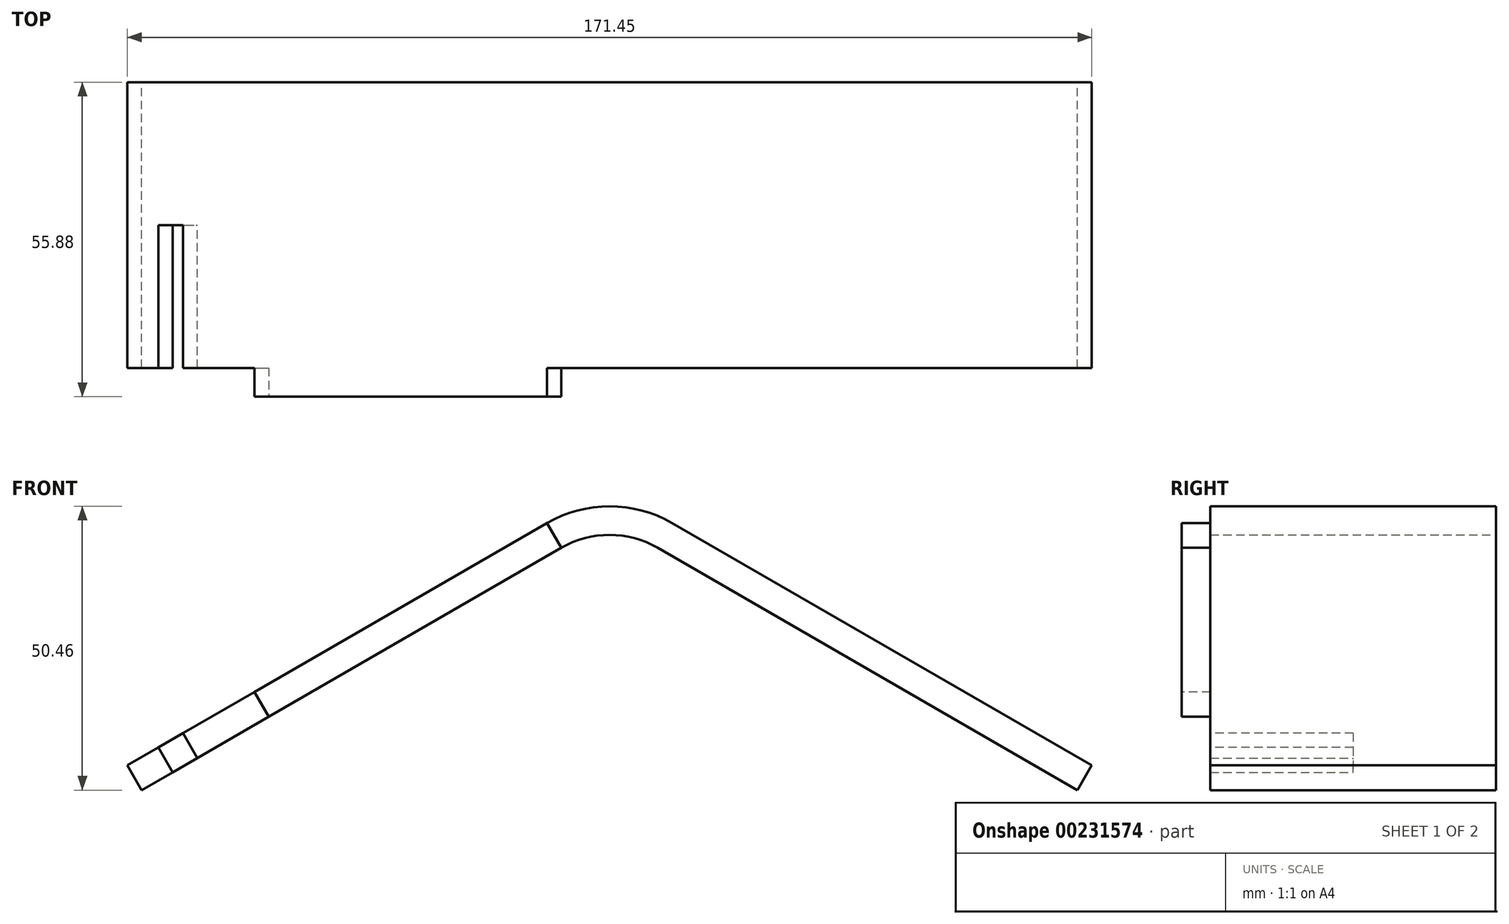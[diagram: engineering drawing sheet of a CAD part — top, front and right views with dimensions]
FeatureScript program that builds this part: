
annotation { "Feature Type Name" : "Feature", "Feature Type Description" : "" }
export const myFeature = defineFeature(function(context is Context, id is Id, definition is map)
    precondition{}
    {
        {
            var Q0;
            Q0=qCreatedBy(makeId("Front.planeOp"),FACE);
            var sketch = newSketch(context, id + "F0", { "sketchPlane" : qUnion([Q0])});
            skLineSegment(sketch, "E0", {"start": v(0, 0) * mm, "end": v(74.61, 43.08) * mm});
            skLineSegment(sketch, "E1", {"start": v(96.84, 43.08) * mm, "end": v(171.45, 0) * mm});
            skPoint(sketch, "E2.visualSharp", {"position": v(85.73, 49.5) * mm});
            skArc(sketch, "E2.filletArc", {"start": v(96.84, 43.08) * mm, "mid": v(85.73, 46.06) * mm, "end": v(74.61, 43.08) * mm});
            skLineSegment(sketch, "E3.0", {"start": v(94.3, 38.68) * mm, "end": v(168.91, -4.4) * mm});
            skArc(sketch, "E3.1", {"start": v(94.3, 38.68) * mm, "mid": v(85.73, 40.98) * mm, "end": v(77.15, 38.68) * mm});
            skLineSegment(sketch, "E3.2", {"start": v(2.54, -4.4) * mm, "end": v(77.15, 38.68) * mm});
            skLineSegment(sketch, "E4", {"start": v(2.54, -4.4) * mm, "end": v(0, 0) * mm});
            skLineSegment(sketch, "E5", {"start": v(168.91, -4.4) * mm, "end": v(171.45, 0) * mm});
            skSolve(sketch);
        }
        {
            var Q0;
            Q0=makeQuery(id+"F0.imprint","IMPRINT",FACE,{"disambiguationData":[TD([[makeQuery(id+"F0.imprint","IMPRINT",EDGE,{"derivedFrom":sQuery(id+"F0.wireOp",EDGE,"E0")}),-1.0]])]});
            extrude(context, id + "F1", {"entities" : qUnion([Q0]), "depth" : 50.8 * mm});
        }
        {
            var Q0;
            Q0=makeQuery(id+"F1.opExtrude","SWEPT_FACE",FACE,{"disambiguationData":[OSD([sQuery(id+"F0.wireOp",EDGE,"E4")])]});
            var Q1;
            Q1=makeQuery(id+"F1.opExtrude","SWEPT_FACE",FACE,{"disambiguationData":[OSD([sQuery(id+"F0.wireOp",EDGE,"E5")])]});
            cPlane(context, id + "F2", {"entities" : qUnion([Q0, Q1]), "cplaneType" : CPlaneType.MID_PLANE, "offset" : 25.4 * mm, "width" : 152.4 * mm, "height" : 152.4 * mm});
        }
        {
            var Q0;
            Q0=makeQuery(id+"F1.opExtrude","CAP_FACE",FACE,{"disambiguationData":[OSD([sQuery(id+"F0.wireOp",EDGE,"E0"),sQuery(id+"F0.wireOp",EDGE,"E1"),sQuery(id+"F0.wireOp",EDGE,"E2.filletArc"),sQuery(id+"F0.wireOp",EDGE,"E3.0"),sQuery(id+"F0.wireOp",EDGE,"E3.1"),sQuery(id+"F0.wireOp",EDGE,"E3.2"),sQuery(id+"F0.wireOp",EDGE,"E4"),sQuery(id+"F0.wireOp",EDGE,"E5")])],"isStart":false});
            var Q1;
            Q1=makeQuery(id+"F1.opExtrude","CAP_FACE",FACE,{"disambiguationData":[OSD([sQuery(id+"F0.wireOp",EDGE,"E0"),sQuery(id+"F0.wireOp",EDGE,"E1"),sQuery(id+"F0.wireOp",EDGE,"E2.filletArc"),sQuery(id+"F0.wireOp",EDGE,"E3.0"),sQuery(id+"F0.wireOp",EDGE,"E3.1"),sQuery(id+"F0.wireOp",EDGE,"E3.2"),sQuery(id+"F0.wireOp",EDGE,"E4"),sQuery(id+"F0.wireOp",EDGE,"E5")])],"isStart":true});
            cPlane(context, id + "F3", {"entities" : qUnion([Q0, Q1]), "cplaneType" : CPlaneType.MID_PLANE, "offset" : 25.4 * mm, "width" : 152.4 * mm, "height" : 152.4 * mm});
        }
        {
            var Q0;
            Q0=makeQuery(id+"F1.opExtrude","SWEPT_FACE",FACE,{"disambiguationData":[OSD([sQuery(id+"F0.wireOp",EDGE,"E3.2")])]});
            var sketch = newSketch(context, id + "F4", { "sketchPlane" : qUnion([Q0])});
            skLineSegment(sketch, "E6.bottom", {"start": v(86.16, 50.8) * mm, "end": v(26.09, 50.8) * mm});
            skLineSegment(sketch, "E6.top", {"start": v(86.16, 55.88) * mm, "end": v(26.09, 55.88) * mm});
            skLineSegment(sketch, "E6.left", {"start": v(86.16, 50.8) * mm, "end": v(86.16, 55.88) * mm});
            skLineSegment(sketch, "E6.right", {"start": v(26.09, 50.8) * mm, "end": v(26.09, 55.88) * mm});
            skSolve(sketch);
        }
        {
            var Q0;
            Q0=makeQuery(id+"F4.imprint","IMPRINT",FACE,{"disambiguationData":[TD([[makeQuery(id+"F4.imprint","IMPRINT",EDGE,{"derivedFrom":sQuery(id+"F4.wireOp",EDGE,"E6.bottom")}),1.0]])]});
            extrude(context, id + "F5", {"entities" : qUnion([Q0]), "operationType" : NewBodyOperationType.ADD, "oppositeDirection" : true, "depth" : 5.08 * mm});
        }
        {
            var Q0;
            {var subQ0=sQuery(id+"F4.wireOp",EDGE,"E6.right");var subQ1=sQuery(id+"F4.wireOp",EDGE,"E6.left");var subQ2=sQuery(id+"F4.wireOp",EDGE,"E6.top");var subQ3=sQuery(id+"F4.wireOp",EDGE,"E6.bottom");Q0=makeQuery(id+"FZIGQqVHOfLiniK_1.1.F5.boolean.opBoolean","MERGE",FACE,{"derivedFrom":[makeQuery(id+"F5.boolean.opBoolean","MERGE",FACE,{"derivedFrom":[makeQuery(id+"F1.opExtrude","SWEPT_FACE",FACE,{"disambiguationData":[OSD([sQuery(id+"F0.wireOp",EDGE,"E3.2")])]}),makeQuery(id+"F5.opExtrude","CAP_FACE",FACE,{"disambiguationData":[OSD([subQ3,subQ2,subQ1,subQ0])],"isStart":true})]}),makeQuery(id+"FZIGQqVHOfLiniK_1.1.F5.opExtrude","CAP_FACE",FACE,{"disambiguationData":[OSD([subQ3,subQ2,subQ1,subQ0])],"isStart":true})]});}
            var sketch = newSketch(context, id + "F6", { "sketchPlane" : qUnion([Q0])});
            skLineSegment(sketch, "E7.bottom", {"start": v(6.35, 50.8) * mm, "end": v(11.43, 50.8) * mm});
            skLineSegment(sketch, "E7.top", {"start": v(6.35, 25.4) * mm, "end": v(11.43, 25.4) * mm});
            skLineSegment(sketch, "E7.left", {"start": v(6.35, 50.8) * mm, "end": v(6.35, 25.4) * mm});
            skLineSegment(sketch, "E7.right", {"start": v(11.43, 50.8) * mm, "end": v(11.43, 25.4) * mm});
            skSolve(sketch);
        }
        {
            var Q0;
            Q0=makeQuery(id+"F6.imprint","IMPRINT",FACE,{"disambiguationData":[TD([[makeQuery(id+"F6.imprint","IMPRINT",EDGE,{"derivedFrom":sQuery(id+"F6.wireOp",EDGE,"E7.bottom")}),-1.0]])]});
            extrude(context, id + "F7", {"entities" : qUnion([Q0]), "operationType" : NewBodyOperationType.REMOVE, "endBound" : BoundingType.THROUGH_ALL, "oppositeDirection" : true, "depth" : 25.4 * mm});
        }
        {
            var Q0;
            {var subQ0=sQuery(id+"F4.wireOp",EDGE,"E6.right");var subQ1=sQuery(id+"F4.wireOp",EDGE,"E6.left");var subQ2=sQuery(id+"F4.wireOp",EDGE,"E6.top");var subQ3=sQuery(id+"F4.wireOp",EDGE,"E6.bottom");Q0=makeQuery(id+"FZIGQqVHOfLiniK_1.1.F5.boolean.opBoolean","MERGE",FACE,{"derivedFrom":[makeQuery(id+"F5.boolean.opBoolean","MERGE",FACE,{"derivedFrom":[makeQuery(id+"F1.opExtrude","SWEPT_FACE",FACE,{"disambiguationData":[OSD([sQuery(id+"F0.wireOp",EDGE,"E3.2")])]}),makeQuery(id+"F5.opExtrude","CAP_FACE",FACE,{"disambiguationData":[OSD([subQ3,subQ2,subQ1,subQ0])],"isStart":true})]}),makeQuery(id+"FZIGQqVHOfLiniK_1.1.F5.opExtrude","CAP_FACE",FACE,{"disambiguationData":[OSD([subQ3,subQ2,subQ1,subQ0])],"isStart":true})]});}
            var sketch = newSketch(context, id + "F8", { "sketchPlane" : qUnion([Q0])});
            skLineSegment(sketch, "E8.bottom", {"start": v(79.8, -5.08) * mm, "end": v(54.4, -5.08) * mm});
            skLineSegment(sketch, "E8.top", {"start": v(79.8, 0) * mm, "end": v(54.4, 0) * mm});
            skLineSegment(sketch, "E8.left", {"start": v(79.8, -5.08) * mm, "end": v(79.8, 0) * mm});
            skLineSegment(sketch, "E8.right", {"start": v(54.4, -5.08) * mm, "end": v(54.4, 0) * mm});
            skSolve(sketch);
        }
        {
            var Q0;
            Q0=makeQuery(id+"F8.imprint","IMPRINT",FACE,{"disambiguationData":[TD([[makeQuery(id+"F8.imprint","IMPRINT",EDGE,{"derivedFrom":sQuery(id+"F8.wireOp",EDGE,"E8.bottom")}),-1.0]])]});
            extrude(context, id + "F9", {"entities" : qUnion([Q0]), "operationType" : NewBodyOperationType.REMOVE, "endBound" : BoundingType.THROUGH_ALL, "oppositeDirection" : true, "depth" : 25.4 * mm});
        }
    });
